# Revit family: Domotics-DomesticRanges-GEWISS-CHORUS_DATA-SOCKET-OUTLET_SELV_POLARIZED
name_source: partatom
category: Apparecchi elettrici
revit_build: Autodesk Revit 2016 (Build: 20161004_0715(x64)
units: mm (PartAtom-declared; Revit-internal decimal feet)

## family parameters
Condiviso = Sì
Host = Superficie
Mantenere orientamento annotazione = Sì
Punto di calcolo locali = Sì
Quota connettore circolare = Usa diametro
Taglio con vuoti quando caricato = Sì
Tipo di parte = Normale

## types (3) — shared parameters
Carico apparente = 0 VA
Catalogue = DOMOTICS
Catalogue Range = CHORUS - DOMESTIC RANGE
Electrocod = 0131
IDF = 2ee08a52-c07b-4216-a952-f92966231962
IDT = 96037f14-3f77-4f7c-ac17-66f6e1a6483f
Immagine tipo = GW14452.jpg
N. poli = 1
Produttore = GEWISS S.p.A.
Prospetto di default = 1219 mm
Technical sheet = https://www.gewiss.com
Tipo_ = SYSTEM PRESE SELV_GENERICO : GW21234 Presa 2P 6A 24V (SELV) polarizzata nero
URL = https://www.gewiss.com
Version file RFA = 19.0
Volt = 230 V

## per-type parameters (varying)
| type | Descrizione | EAN code | Modello |
| GW10452 - SELV SOCKET 2P 6A 24V POLARISED 1M WHITE | SELV SOCKET 2P 6A 24V POLARISED 1M WHITE | 8011564262638 | GW10452 |
| GW12452 - SELV SOCKET 2P 6A 24V POLARISED 1M BLACK | SELV SOCKET 2P 6A 24V POLARISED 1M BLACK | 8011564269651 | GW12452 |
| GW14452 - SELV SOCKET, 2P 6A 24V POLARISED 1M T | SELV SOCKET, 2P 6A 24V POLARISED 1M T | 8011564267626 | GW14452 |

## geometry (parser evidence)
native form markers: Sweep x2
no freeform markers — native parametric forms only
